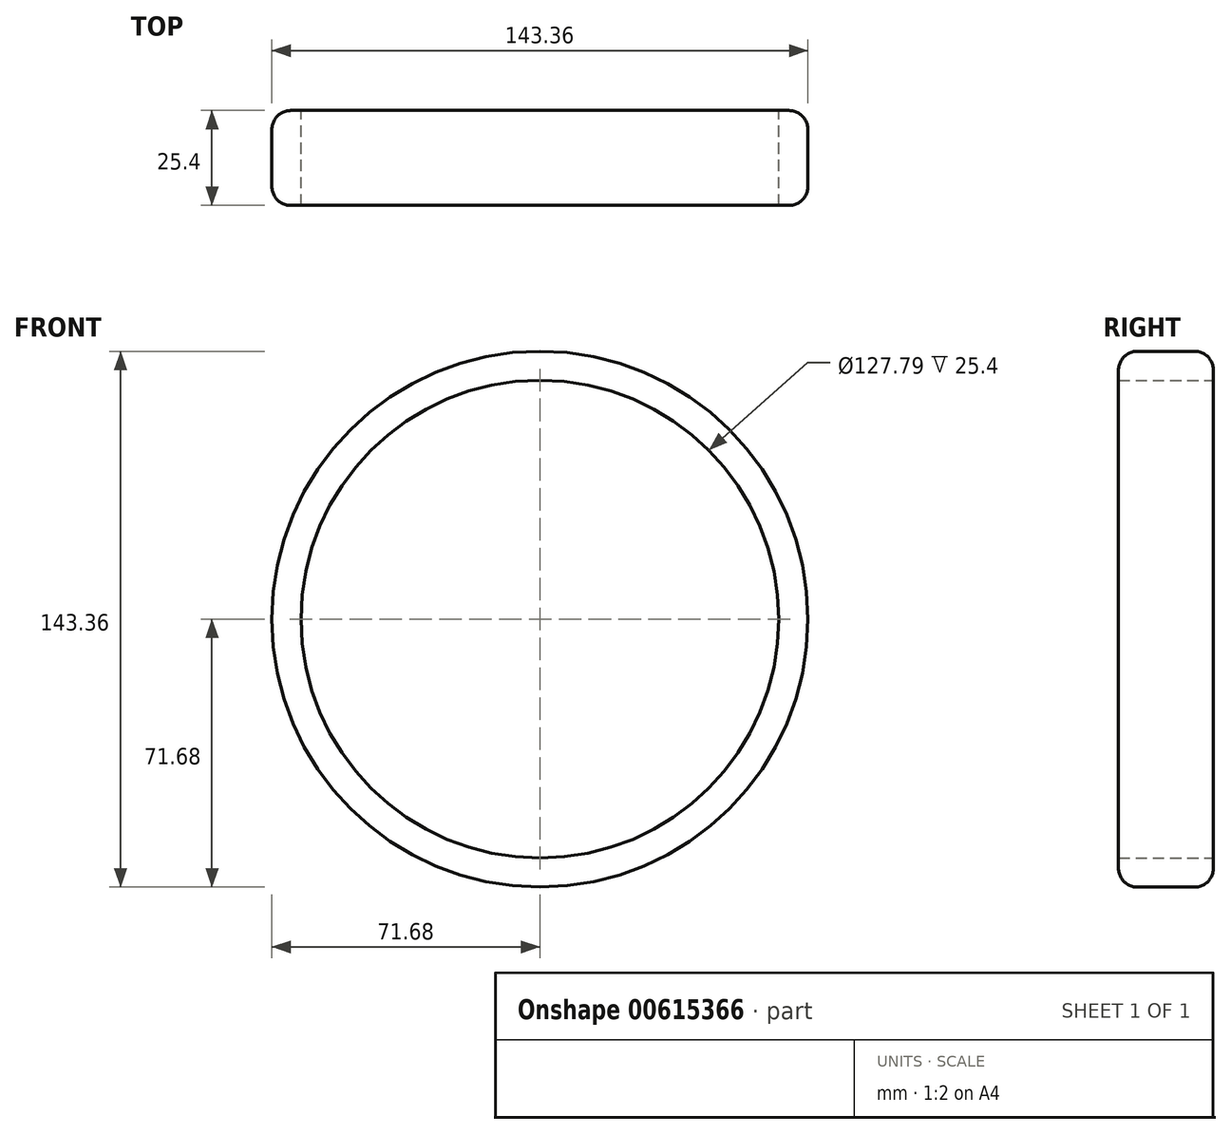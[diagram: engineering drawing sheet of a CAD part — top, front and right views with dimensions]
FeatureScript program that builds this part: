
annotation { "Feature Type Name" : "Feature", "Feature Type Description" : "" }
export const myFeature = defineFeature(function(context is Context, id is Id, definition is map)
    precondition{}
    {
        {
            var Q0;
            Q0=qCreatedBy(makeId("Front.planeOp"),FACE);
            var sketch = newSketch(context, id + "F0", { "sketchPlane" : qUnion([Q0])});
            skCircle(sketch, "E0", {"center": v(0, 0) * mm, "radius": 71.68 * mm});
            skCircle(sketch, "E1", {"center": v(0, 0) * mm, "radius": 63.9 * mm});
            skSolve(sketch);
        }
        {
            var Q0;
            Q0=makeQuery(id+"F0.imprint","IMPRINT",FACE,{"disambiguationData":[TD([[makeQuery(id+"F0.imprint","IMPRINT",EDGE,{"derivedFrom":sQuery(id+"F0.wireOp",EDGE,"E0")}),1.0]])]});
            extrude(context, id + "F1", {"entities" : qUnion([Q0]), "endBound" : BoundingType.SYMMETRIC, "depth" : 25.4 * mm, "offsetDistance" : 25.4 * mm});
        }
        {
            var Q0;
            Q0=makeQuery(id+"F1.opExtrude","SWEPT_FACE",FACE,{"disambiguationData":[OSD([sQuery(id+"F0.wireOp",EDGE,"E0")])]});
            fillet(context, id + "F2", {"entities" : qUnion([Q0]), "radius" : 5.08 * mm, "tangentPropagation" : true, "allowEdgeOverflow" : false});
        }
    });
